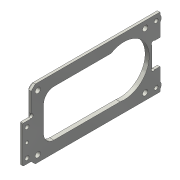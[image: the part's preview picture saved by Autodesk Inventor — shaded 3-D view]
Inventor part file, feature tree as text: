
AUTODESK INVENTOR PART (.ipt)
format: ipt  version: 2019.4 (Build 234330000, 330)  size: 285,184 bytes
history: native  units: mm
features: sketch x4, extrude x4, hole x3, other x1, chamfer x1
ambient origin geometry x8: Origin, YZ Plane, XZ Plane, XY Plane, X Axis, Y Axis, Z Axis, Center Point
bodies: Body1 (feature_tree)
feature tree (13):
  other  "ソリッド1"
  sketch  "スケッチ1"
  extrude  "押し出し1"  Depth=12.2mm
  extrude  "押し出し2"  Depth=33.5mm
  hole  "穴1"  [1 undecoded]
  hole  "穴2"  [1 undecoded]
  extrude  "押し出し3"  Depth=2.0mm
  hole  "穴3"  [1 undecoded]
  extrude  "押し出し4"  Depth=2.0mm
  chamfer  "面取り1"  Distance=2.0mm
  sketch  "スケッチ2"
  sketch  "スケッチ3"
  sketch  "スケッチ4"
note: 3 required parameter values undecoded (feature->parameter linkage not recoverable at this tier; creation-order binding heuristic only, values carry confidence <= 0.55)
